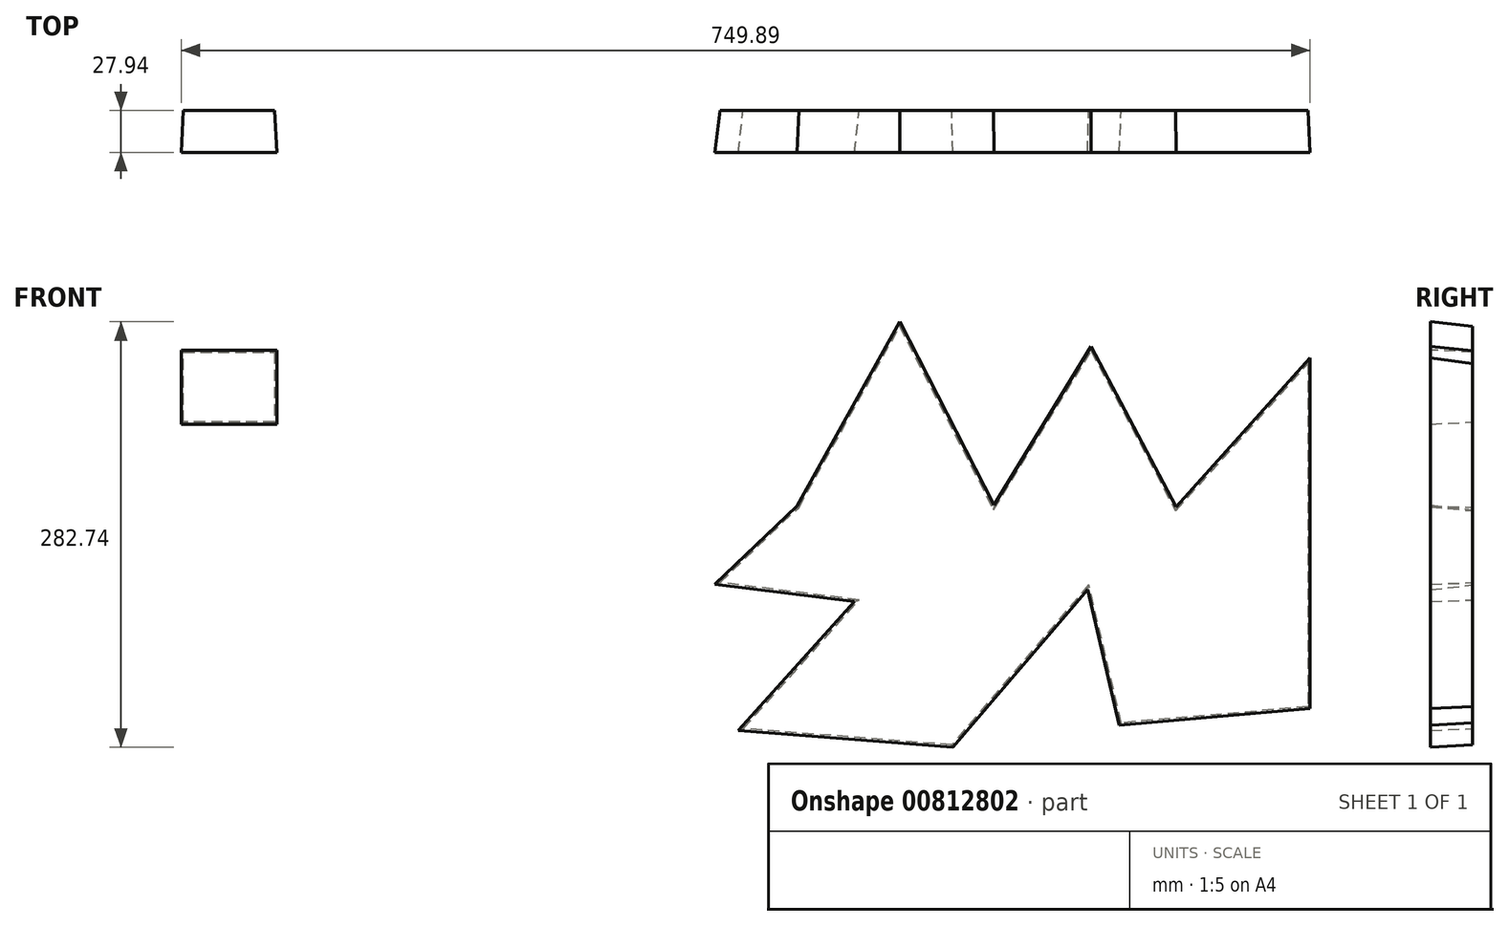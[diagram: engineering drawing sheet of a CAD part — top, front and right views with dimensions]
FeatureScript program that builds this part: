
annotation { "Feature Type Name" : "Feature", "Feature Type Description" : "" }
export const myFeature = defineFeature(function(context is Context, id is Id, definition is map)
    precondition{}
    {
        {
            var Q0;
            Q0=qCreatedBy(makeId("Front.planeOp"),FACE);
            var sketch = newSketch(context, id + "F0", { "sketchPlane" : qUnion([Q0])});
            skLineSegment(sketch, "E0.bottom", {"start": v(-147.95, 46.29) * mm, "end": v(-87.38, 46.29) * mm});
            skLineSegment(sketch, "E0.top", {"start": v(-147.95, 0) * mm, "end": v(-87.38, 0) * mm});
            skLineSegment(sketch, "E0.left", {"start": v(-147.95, 46.29) * mm, "end": v(-147.95, 0) * mm});
            skLineSegment(sketch, "E0.right", {"start": v(-87.38, 46.29) * mm, "end": v(-87.38, 0) * mm});
            skLineSegment(sketch, "E1", {"start": v(176.96, -353.82) * mm, "end": v(226.8, -299.74) * mm, "construction": true});
            skPoint(sketch, "E2", {"position": v(-330.94, -180.27) * mm});
            skPoint(sketch, "E3", {"position": v(-238.05, -127.71) * mm});
            skPoint(sketch, "E4.0.1.0", {"position": v(-238.05, -232.62) * mm});
            skPoint(sketch, "E4.0.1.1", {"position": v(-330.94, -285.17) * mm});
            skLineSegment(sketch, "E4.0.1.2", {"start": v(176.96, -458.72) * mm, "end": v(226.8, -404.64) * mm, "construction": true});
            skPoint(sketch, "E4.1.0.0", {"position": v(-132.38, -127.71) * mm});
            skPoint(sketch, "E4.1.0.1", {"position": v(-225.28, -180.27) * mm});
            skLineSegment(sketch, "E4.1.0.2", {"start": v(282.62, -353.82) * mm, "end": v(332.46, -299.74) * mm, "construction": true});
            skPoint(sketch, "E4.1.1.0", {"position": v(-132.38, -232.62) * mm});
            skPoint(sketch, "E4.1.1.1", {"position": v(-225.28, -285.17) * mm});
            skLineSegment(sketch, "E4.1.1.2", {"start": v(282.62, -458.72) * mm, "end": v(332.46, -404.64) * mm, "construction": true});
            skPoint(sketch, "E4.2.0.0", {"position": v(-26.72, -127.71) * mm});
            skPoint(sketch, "E4.2.0.1", {"position": v(-119.61, -180.27) * mm});
            skLineSegment(sketch, "E4.2.0.2", {"start": v(388.29, -353.82) * mm, "end": v(438.13, -299.74) * mm});
            skPoint(sketch, "E4.2.1.0", {"position": v(-26.72, -232.62) * mm});
            skPoint(sketch, "E4.2.1.1", {"position": v(-119.61, -285.17) * mm});
            skLineSegment(sketch, "E4.2.1.2", {"start": v(388.29, -458.72) * mm, "end": v(438.13, -404.64) * mm, "construction": true});
            skLineSegment(sketch, "E4.direction1", {"start": v(176.96, -353.82) * mm, "end": v(282.62, -353.82) * mm, "construction": true});
            skLineSegment(sketch, "E4.direction2", {"start": v(176.96, -353.82) * mm, "end": v(176.96, -458.72) * mm, "construction": true});
            skLineSegment(sketch, "E5", {"start": v(-330.94, -180.27) * mm, "end": v(-238.05, -127.71) * mm, "construction": true});
            skLineSegment(sketch, "E6", {"start": v(-238.05, -127.71) * mm, "end": v(-225.28, -180.27) * mm, "construction": true});
            skLineSegment(sketch, "E7", {"start": v(-132.38, -127.71) * mm, "end": v(-225.28, -180.27) * mm, "construction": true});
            skLineSegment(sketch, "E8", {"start": v(-132.38, -127.71) * mm, "end": v(-119.61, -180.27) * mm, "construction": true});
            skLineSegment(sketch, "E9", {"start": v(-119.61, -180.27) * mm, "end": v(-26.72, -127.71) * mm, "construction": true});
            skLineSegment(sketch, "E10", {"start": v(-26.72, -127.71) * mm, "end": v(-26.72, -232.62) * mm});
            skLineSegment(sketch, "E11", {"start": v(-26.72, -232.62) * mm, "end": v(-132.38, -232.62) * mm, "construction": true});
            skLineSegment(sketch, "E12", {"start": v(-119.61, -285.17) * mm, "end": v(-132.38, -232.62) * mm, "construction": true});
            skLineSegment(sketch, "E13", {"start": v(-119.61, -285.17) * mm, "end": v(-225.28, -285.17) * mm, "construction": true});
            skLineSegment(sketch, "E14", {"start": v(-225.28, -285.17) * mm, "end": v(-238.05, -232.62) * mm, "construction": true});
            skLineSegment(sketch, "E15", {"start": v(-330.94, -285.17) * mm, "end": v(-238.05, -232.62) * mm, "construction": true});
            skLineSegment(sketch, "E16", {"start": v(-330.94, -180.27) * mm, "end": v(-330.94, -285.17) * mm, "construction": true});
            skLineSegment(sketch, "E17", {"start": v(260.8, -56.73) * mm, "end": v(327.82, 63.46) * mm});
            skLineSegment(sketch, "E18", {"start": v(327.82, 63.46) * mm, "end": v(390.22, -58.27) * mm});
            skLineSegment(sketch, "E19", {"start": v(390.22, -58.27) * mm, "end": v(454.94, 47.28) * mm});
            skLineSegment(sketch, "E20", {"start": v(454.94, 47.28) * mm, "end": v(511.18, -59.04) * mm});
            skLineSegment(sketch, "E21", {"start": v(511.18, -59.04) * mm, "end": v(599.01, 38.8) * mm});
            skLineSegment(sketch, "E22", {"start": v(599.01, 38.8) * mm, "end": v(599.01, -189.24) * mm});
            skLineSegment(sketch, "E23", {"start": v(599.01, -189.24) * mm, "end": v(474.97, -200.03) * mm});
            skLineSegment(sketch, "E24", {"start": v(474.97, -200.03) * mm, "end": v(453.4, -108.35) * mm});
            skLineSegment(sketch, "E25", {"start": v(453.4, -108.35) * mm, "end": v(362.49, -214.67) * mm});
            skLineSegment(sketch, "E26", {"start": v(362.49, -214.67) * mm, "end": v(223.81, -203.88) * mm});
            skLineSegment(sketch, "E27", {"start": v(223.81, -203.88) * mm, "end": v(300.85, -118.36) * mm});
            skLineSegment(sketch, "E28", {"start": v(300.85, -118.36) * mm, "end": v(208.4, -106.8) * mm});
            skLineSegment(sketch, "E29", {"start": v(208.4, -106.8) * mm, "end": v(260.8, -56.73) * mm});
            skSolve(sketch);
        }
        {
            var Q0;
            Q0=makeQuery(id+"F0.imprint","IMPRINT",FACE,{"disambiguationData":[TD([[makeQuery(id+"F0.imprint","IMPRINT",EDGE,{"derivedFrom":sQuery(id+"F0.wireOp",EDGE,"E17")}),-1.0]])]});
            var Q1;
            Q1=makeQuery(id+"F0.imprint","IMPRINT",FACE,{"disambiguationData":[TD([[makeQuery(id+"F0.imprint","IMPRINT",EDGE,{"derivedFrom":sQuery(id+"F0.wireOp",EDGE,"E0.bottom")}),-1.0]])]});
            extrude(context, id + "F1", {"entities" : qUnion([Q0, Q1]), "depth" : 27.94 * mm, "offsetDistance" : 25.4 * mm, "hasDraft" : true, "draftAngle" : 0.05 * radian});
        }
    });
